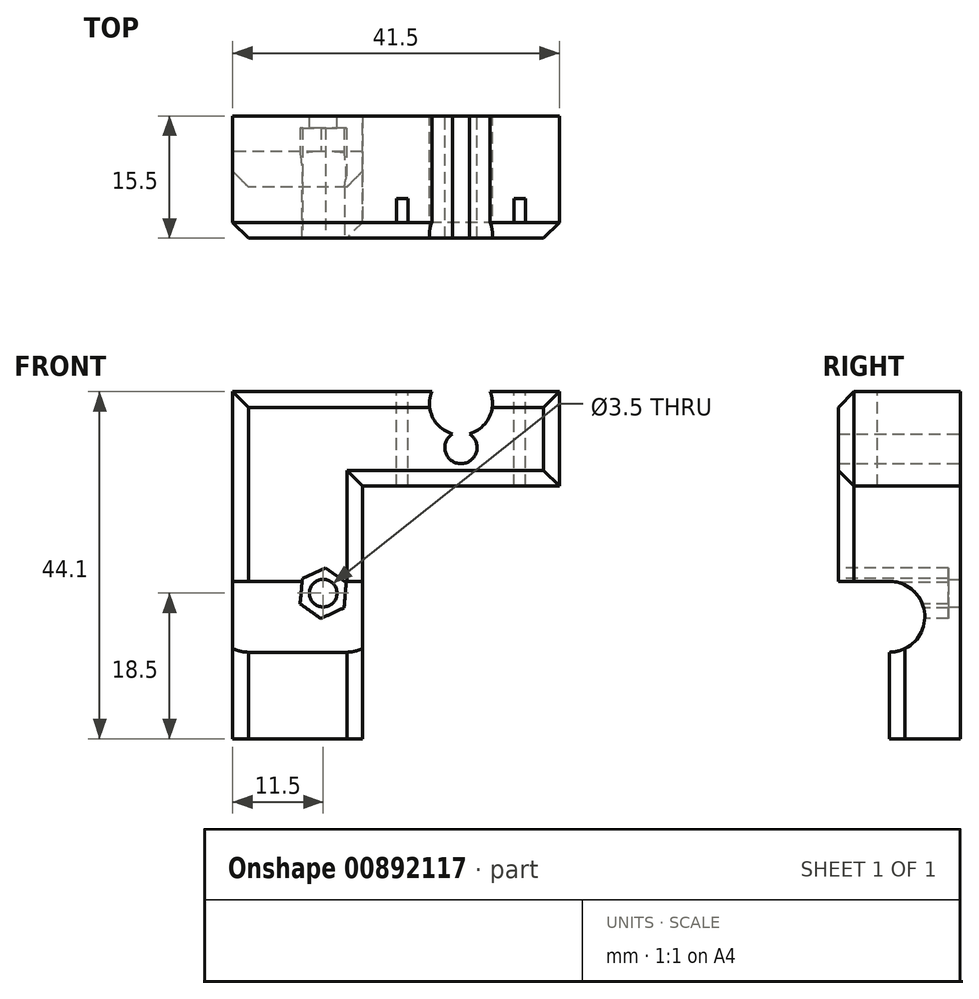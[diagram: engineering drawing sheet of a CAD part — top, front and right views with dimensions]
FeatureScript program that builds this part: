
annotation { "Feature Type Name" : "Feature", "Feature Type Description" : "" }
export const myFeature = defineFeature(function(context is Context, id is Id, definition is map)
    precondition{}
    {
        {
            var Q0;
            Q0=qCreatedBy(makeId("Front.planeOp"),FACE);
            var sketch = newSketch(context, id + "F0", { "sketchPlane" : qUnion([Q0])});
            skLineSegment(sketch, "E0.right", {"start": v(16.5, 21.37) * mm, "end": v(16.5, 38.5) * mm});
            skPoint(sketch, "E1.centerSnap0", {"position": v(8.25, 38.5) * mm});
            skLineSegment(sketch, "E2.trimOffspring", {"start": v(10.09, 38.5) * mm, "end": v(10.09, 38.5) * mm});
            skLineSegment(sketch, "E3", {"start": v(0, 38.5) * mm, "end": v(0, 21.37) * mm});
            skPoint(sketch, "E4.start.orphan", {"position": v(8.25, 33.37) * mm});
            skPoint(sketch, "E5.center.orphan", {"position": v(8.25, 37) * mm});
            skPoint(sketch, "E6.end.orphan", {"position": v(8.25, 21.37) * mm});
            skLineSegment(sketch, "E7", {"start": v(0, 38.5) * mm, "end": v(4.54, 38.5) * mm});
            skArc(sketch, "E8", {"start": v(4.54, 38.5) * mm, "mid": v(4.65, 35.25) * mm, "end": v(7.13, 33.16) * mm});
            skLineSegment(sketch, "E9.trimOffspring", {"start": v(11.96, 38.5) * mm, "end": v(16.5, 38.5) * mm});
            skArc(sketch, "E10", {"start": v(7.13, 33.16) * mm, "mid": v(8.25, 29.4) * mm, "end": v(9.37, 33.16) * mm});
            skArc(sketch, "E11.trimOffspring", {"start": v(9.37, 33.16) * mm, "mid": v(11.85, 35.25) * mm, "end": v(11.96, 38.5) * mm});
            skLineSegment(sketch, "E12", {"start": v(8.25, 21) * mm, "end": v(16.5, 21) * mm});
            skLineSegment(sketch, "E13", {"start": v(16.5, 21) * mm, "end": v(16.5, 21.37) * mm});
            skLineSegment(sketch, "E14", {"start": v(8.25, 21) * mm, "end": v(0, 21) * mm});
            skLineSegment(sketch, "E15", {"start": v(0, 21) * mm, "end": v(0, 21.37) * mm});
            skSolve(sketch);
        }
        {
            var Q0;
            Q0=qSketchRegion(id+"F0",true);
            extrude(context, id + "F1", {"entities" : qUnion([Q0]), "depth" : 17.5 * mm});
        }
        {
            var Q0;
            Q0=makeQuery(id+"F1.opExtrude","CAP_FACE",FACE,{"disambiguationData":[OSD([sQuery(id+"F0.wireOp",EDGE,"E0.right"),sQuery(id+"F0.wireOp",EDGE,"E3"),sQuery(id+"F0.wireOp",EDGE,"E7"),sQuery(id+"F0.wireOp",EDGE,"E8"),sQuery(id+"F0.wireOp",EDGE,"E9.trimOffspring"),sQuery(id+"F0.wireOp",EDGE,"E10"),sQuery(id+"F0.wireOp",EDGE,"E11.trimOffspring"),sQuery(id+"F0.wireOp",EDGE,"E12"),sQuery(id+"F0.wireOp",EDGE,"E13"),sQuery(id+"F0.wireOp",EDGE,"E14"),sQuery(id+"F0.wireOp",EDGE,"E15")])],"isStart":true});
            var sketch = newSketch(context, id + "F2", { "sketchPlane" : qUnion([Q0])});
            skLineSegment(sketch, "E16.bottom", {"start": v(-16.5, 21) * mm, "end": v(0, 21) * mm});
            skLineSegment(sketch, "E16.top", {"start": v(-16.5, 1) * mm, "end": v(0, 1) * mm});
            skLineSegment(sketch, "E16.left", {"start": v(-16.5, 21) * mm, "end": v(-16.5, 1) * mm});
            skLineSegment(sketch, "E16.right", {"start": v(0, 21) * mm, "end": v(0, 1) * mm});
            skSolve(sketch);
        }
        {
            var Q0;
            Q0=makeQuery(id+"F2.imprint","IMPRINT",FACE,{"disambiguationData":[TD([[makeQuery(id+"F2.imprint","IMPRINT",EDGE,{"derivedFrom":sQuery(id+"F2.wireOp",EDGE,"E16.bottom")}),-1.0]])]});
            extrude(context, id + "F3", {"entities" : qUnion([Q0]), "operationType" : NewBodyOperationType.ADD, "oppositeDirection" : true, "depth" : 11 * mm});
        }
        {
            var Q0;
            Q0=makeQuery(id+"F3.boolean.opBoolean","MERGE",FACE,{"derivedFrom":[makeQuery(id+"F1.opExtrude","CAP_FACE",FACE,{"disambiguationData":[OSD([sQuery(id+"F0.wireOp",EDGE,"E0.right"),sQuery(id+"F0.wireOp",EDGE,"E3"),sQuery(id+"F0.wireOp",EDGE,"E7"),sQuery(id+"F0.wireOp",EDGE,"E8"),sQuery(id+"F0.wireOp",EDGE,"E9.trimOffspring"),sQuery(id+"F0.wireOp",EDGE,"E10"),sQuery(id+"F0.wireOp",EDGE,"E11.trimOffspring"),sQuery(id+"F0.wireOp",EDGE,"E12"),sQuery(id+"F0.wireOp",EDGE,"E13"),sQuery(id+"F0.wireOp",EDGE,"E14"),sQuery(id+"F0.wireOp",EDGE,"E15")])],"isStart":true}),makeQuery(id+"F3.opExtrude","CAP_FACE",FACE,{"disambiguationData":[OSD([sQuery(id+"F2.wireOp",EDGE,"E16.bottom"),sQuery(id+"F2.wireOp",EDGE,"E16.top"),sQuery(id+"F2.wireOp",EDGE,"E16.left"),sQuery(id+"F2.wireOp",EDGE,"E16.right")])],"isStart":true})]});
            var sketch = newSketch(context, id + "F4", { "sketchPlane" : qUnion([Q0])});
            skPoint(sketch, "E17.endSnap0", {"position": v(-8.25, 29.4) * mm});
            skCircle(sketch, "E18", {"center": v(-11.5, 19.5) * mm, "radius": 1.75 * mm});
            skPoint(sketch, "E19.orphan", {"position": v(-16.5, 19.5) * mm});
            skPoint(sketch, "E20.end.orphan", {"position": v(-8.25, 19.5) * mm});
            skSolve(sketch);
        }
        {
            var Q0;
            Q0=makeQuery(id+"F3.boolean.opBoolean","MERGE",FACE,{"derivedFrom":[makeQuery(id+"F1.opExtrude","SWEPT_FACE",FACE,{"disambiguationData":[OSD([sQuery(id+"F0.wireOp",EDGE,"E3"),sQuery(id+"F0.wireOp",EDGE,"E15")])]}),makeQuery(id+"F3.opExtrude","SWEPT_FACE",FACE,{"disambiguationData":[OSD([sQuery(id+"F2.wireOp",EDGE,"E16.right")])]})]});
            var sketch = newSketch(context, id + "F5", { "sketchPlane" : qUnion([Q0])});
            skLineSegment(sketch, "E21", {"start": v(11, 21) * mm, "end": v(11, 16.5) * mm});
            skArc(sketch, "E22", {"start": v(11, 21) * mm, "mid": v(6.5, 16.5) * mm, "end": v(11, 12) * mm});
            skLineSegment(sketch, "E23", {"start": v(11, 16.5) * mm, "end": v(11, 12) * mm});
            skPoint(sketch, "E24.orphan", {"position": v(11, 11) * mm});
            skSolve(sketch);
        }
        {
            var Q0;
            Q0=qSketchRegion(id+"F4",true);
            extrude(context, id + "F6", {"entities" : qUnion([Q0]), "operationType" : NewBodyOperationType.REMOVE, "oppositeDirection" : true, "depth" : 22.5 * mm});
        }
        {
            var Q0;
            Q0=makeQuery(id+"F3.opExtrude","CAP_FACE",FACE,{"disambiguationData":[OSD([sQuery(id+"F2.wireOp",EDGE,"E16.bottom"),sQuery(id+"F2.wireOp",EDGE,"E16.top"),sQuery(id+"F2.wireOp",EDGE,"E16.left"),sQuery(id+"F2.wireOp",EDGE,"E16.right")])],"isStart":false});
            var sketch = newSketch(context, id + "F7", { "sketchPlane" : qUnion([Q0])});
            skCircle(sketch, "E25.cCircle", {"center": v(11.5, 19.5) * mm, "radius": 2.8 * mm, "construction": true});
            skLineSegment(sketch, "E25.0", {"start": v(14.43, 20.86) * mm, "end": v(14.14, 17.64) * mm});
            skLineSegment(sketch, "E25.1", {"start": v(14.14, 17.64) * mm, "end": v(11.2, 16.28) * mm});
            skLineSegment(sketch, "E25.2", {"start": v(11.2, 16.28) * mm, "end": v(8.57, 18.14) * mm});
            skLineSegment(sketch, "E25.3", {"start": v(8.57, 18.14) * mm, "end": v(8.86, 21.36) * mm});
            skLineSegment(sketch, "E25.4", {"start": v(8.86, 21.36) * mm, "end": v(11.8, 22.72) * mm});
            skLineSegment(sketch, "E25.5", {"start": v(11.8, 22.72) * mm, "end": v(14.43, 20.86) * mm});
            skPoint(sketch, "E25.0.midPoint", {"position": v(14.29, 19.25) * mm});
            skSolve(sketch);
        }
        {
            var Q0;
            Q0=qSketchRegion(id+"F7",true);
            extrude(context, id + "F8", {"entities" : qUnion([Q0]), "operationType" : NewBodyOperationType.REMOVE, "oppositeDirection" : true, "depth" : 7.5 * mm});
        }
        {
            var Q0;
            Q0=qSketchRegion(id+"F7",true);
            extrude(context, id + "F9", {"entities" : qUnion([Q0]), "operationType" : NewBodyOperationType.REMOVE, "depth" : 13.1 * mm});
        }
        {
            var Q0;
            Q0=qSketchRegion(id+"F5",true);
            extrude(context, id + "F10", {"entities" : qUnion([Q0]), "operationType" : NewBodyOperationType.REMOVE, "oppositeDirection" : true, "depth" : 24.9 * mm});
        }
        {
            var Q0;
            Q0=makeQuery(id+"F3.boolean.opBoolean","MERGE",FACE,{"derivedFrom":[makeQuery(id+"F1.opExtrude","CAP_FACE",FACE,{"disambiguationData":[OSD([sQuery(id+"F0.wireOp",EDGE,"E0.right"),sQuery(id+"F0.wireOp",EDGE,"E3"),sQuery(id+"F0.wireOp",EDGE,"E7"),sQuery(id+"F0.wireOp",EDGE,"E8"),sQuery(id+"F0.wireOp",EDGE,"E9.trimOffspring"),sQuery(id+"F0.wireOp",EDGE,"E10"),sQuery(id+"F0.wireOp",EDGE,"E11.trimOffspring"),sQuery(id+"F0.wireOp",EDGE,"E12"),sQuery(id+"F0.wireOp",EDGE,"E13"),sQuery(id+"F0.wireOp",EDGE,"E14"),sQuery(id+"F0.wireOp",EDGE,"E15")])],"isStart":true}),makeQuery(id+"F3.opExtrude","CAP_FACE",FACE,{"disambiguationData":[OSD([sQuery(id+"F2.wireOp",EDGE,"E16.bottom"),sQuery(id+"F2.wireOp",EDGE,"E16.top"),sQuery(id+"F2.wireOp",EDGE,"E16.left"),sQuery(id+"F2.wireOp",EDGE,"E16.right")])],"isStart":true})]});
            var sketch = newSketch(context, id + "F11", { "sketchPlane" : qUnion([Q0])});
            skLineSegment(sketch, "E26", {"start": v(-16.5, 38.5) * mm, "end": v(-16.5, 1) * mm});
            skLineSegment(sketch, "E27", {"start": v(-16.5, 1) * mm, "end": v(0, 1) * mm});
            skLineSegment(sketch, "E28", {"start": v(0, 1) * mm, "end": v(0, 38.5) * mm});
            skLineSegment(sketch, "E29", {"start": v(0, 38.5) * mm, "end": v(-4.54, 38.5) * mm});
            skLineSegment(sketch, "E30", {"start": v(-11.96, 38.5) * mm, "end": v(-16.5, 38.5) * mm});
            skArc(sketch, "E31", {"start": v(-11.96, 38.5) * mm, "mid": v(-11.85, 35.25) * mm, "end": v(-9.37, 33.16) * mm});
            skArc(sketch, "E32", {"start": v(-9.37, 33.16) * mm, "mid": v(-8.25, 29.4) * mm, "end": v(-7.13, 33.16) * mm});
            skArc(sketch, "E33.trimOffspring", {"start": v(-7.13, 33.16) * mm, "mid": v(-4.65, 35.25) * mm, "end": v(-4.54, 38.5) * mm});
            skSolve(sketch);
        }
        {
            var Q0;
            Q0=makeQuery(id+"F11.imprint","IMPRINT",FACE,{"disambiguationData":[TD([[makeQuery(id+"F11.imprint","IMPRINT",EDGE,{"derivedFrom":sQuery(id+"F11.wireOp",EDGE,"E26")}),-1.0]])]});
            extrude(context, id + "F12", {"entities" : qUnion([Q0]), "operationType" : NewBodyOperationType.REMOVE, "oppositeDirection" : true, "depth" : 2 * mm});
        }
        {
            var Q0;
            Q0=makeQuery(id+"F3.boolean.opBoolean","MERGE",FACE,{"derivedFrom":[makeQuery(id+"F1.opExtrude","SWEPT_FACE",FACE,{"disambiguationData":[OSD([sQuery(id+"F0.wireOp",EDGE,"E0.right"),sQuery(id+"F0.wireOp",EDGE,"E13")])]}),makeQuery(id+"F3.opExtrude","SWEPT_FACE",FACE,{"disambiguationData":[OSD([sQuery(id+"F2.wireOp",EDGE,"E16.left")])]})]});
            var sketch = newSketch(context, id + "F13", { "sketchPlane" : qUnion([Q0])});
            skLineSegment(sketch, "E34.top", {"start": v(-2, 33.1) * mm, "end": v(-17.5, 33.1) * mm});
            skLineSegment(sketch, "E34.left", {"start": v(-2, 38.5) * mm, "end": v(-2, 33.1) * mm});
            skLineSegment(sketch, "E34.right", {"start": v(-17.5, 38.5) * mm, "end": v(-17.5, 33.1) * mm});
            skLineSegment(sketch, "E35.top", {"start": v(-2, 45.1) * mm, "end": v(-17.5, 45.1) * mm});
            skLineSegment(sketch, "E35.left", {"start": v(-2, 38.5) * mm, "end": v(-2, 45.1) * mm});
            skLineSegment(sketch, "E35.right", {"start": v(-17.5, 38.5) * mm, "end": v(-17.5, 45.1) * mm});
            skSolve(sketch);
        }
        {
            var Q0;
            Q0=makeQuery(id+"F13.imprint","IMPRINT",FACE,{"disambiguationData":[TD([[makeQuery(id+"F13.imprint","IMPRINT",EDGE,{"derivedFrom":sQuery(id+"F13.wireOp",EDGE,"E35.top")}),1.0]])]});
            var Q1;
            Q1=makeQuery(id+"F13.imprint","IMPRINT",FACE,{"disambiguationData":[TD([[makeQuery(id+"F13.imprint","IMPRINT",EDGE,{"derivedFrom":sQuery(id+"F13.wireOp",EDGE,"E34.top")}),-1.0]])]});
            extrude(context, id + "F14", {"entities" : qUnion([Q0, Q1]), "operationType" : NewBodyOperationType.ADD, "depth" : 25 * mm});
        }
        {
            var Q0;
            Q0=makeQuery(id+"F14.opExtrude","CAP_FACE",FACE,{"disambiguationData":[OSD([sQuery(id+"F13.wireOp",EDGE,"E34.top"),sQuery(id+"F13.wireOp",EDGE,"E34.left"),sQuery(id+"F13.wireOp",EDGE,"E34.right"),sQuery(id+"F13.wireOp",EDGE,"E35.top"),sQuery(id+"F13.wireOp",EDGE,"E35.left"),sQuery(id+"F13.wireOp",EDGE,"E35.right")])],"isStart":true});
            extrude(context, id + "F15", {"entities" : qUnion([Q0]), "operationType" : NewBodyOperationType.ADD, "depth" : 16.5 * mm});
        }
        {
            var Q0;
            {var subQ0=sQuery(id+"F13.wireOp",EDGE,"E35.left");var subQ1=sQuery(id+"F13.wireOp",EDGE,"E34.left");Q0=makeQuery(id+"F15.boolean.opBoolean","MERGE",FACE,{"derivedFrom":[makeQuery(id+"F14.boolean.opBoolean","MERGE",FACE,{"derivedFrom":[makeQuery(id+"F12.boolean.opBoolean","COPY",FACE,{"derivedFrom":makeQuery(id+"F12.opExtrude","CAP_FACE",FACE,{"disambiguationData":[OSD([sQuery(id+"F4.wireOp",EDGE,"E18"),sQuery(id+"F11.wireOp",EDGE,"E26"),sQuery(id+"F11.wireOp",EDGE,"E27"),sQuery(id+"F11.wireOp",EDGE,"E28"),sQuery(id+"F11.wireOp",EDGE,"E29"),sQuery(id+"F11.wireOp",EDGE,"E30"),sQuery(id+"F11.wireOp",EDGE,"E31"),sQuery(id+"F11.wireOp",EDGE,"E32"),sQuery(id+"F11.wireOp",EDGE,"E33.trimOffspring")])],"isStart":false})}),makeQuery(id+"F14.opExtrude","SWEPT_FACE",FACE,{"disambiguationData":[OSD([subQ1,subQ0])]})]}),makeQuery(id+"F15.opExtrude","SWEPT_FACE",FACE,{"disambiguationData":[OSD([subQ1,subQ0])]})]});}
            var sketch = newSketch(context, id + "F16", { "sketchPlane" : qUnion([Q0])});
            skPoint(sketch, "E36.endSnap0", {"position": v(-29, 45.1) * mm});
            skArc(sketch, "E37", {"start": v(-27.93, 39.74) * mm, "mid": v(-25.4, 41.83) * mm, "end": v(-25.3, 45.1) * mm});
            skPoint(sketch, "E36.start.orphan", {"position": v(-29, 45.1) * mm});
            skArc(sketch, "E38", {"start": v(-30.07, 39.74) * mm, "mid": v(-29, 35.94) * mm, "end": v(-27.93, 39.74) * mm});
            skArc(sketch, "E39.trimOffspring", {"start": v(-32.7, 45.1) * mm, "mid": v(-32.6, 41.83) * mm, "end": v(-30.07, 39.74) * mm});
            skPoint(sketch, "E40.trimOffspring.end.orphan", {"position": v(-41.5, 45.1) * mm});
            skPoint(sketch, "E41.start.orphan", {"position": v(-16.5, 45.1) * mm});
            skLineSegment(sketch, "E42", {"start": v(-32.7, 45.1) * mm, "end": v(-25.3, 45.1) * mm});
            skSolve(sketch);
        }
        {
            var Q0;
            Q0=qSketchRegion(id+"F16",true);
            extrude(context, id + "F17", {"entities" : qUnion([Q0]), "operationType" : NewBodyOperationType.REMOVE, "oppositeDirection" : true, "depth" : 25 * mm});
        }
        {
            var Q0;
            {var subQ6=sQuery(id+"F13.wireOp",EDGE,"E35.top");Q0=makeQuery(id+"F17.boolean.opBoolean","SPLIT",FACE,{"disambiguationData":[TD([makeQuery(id+"F3.opExtrude","SWEPT_FACE",FACE,{"disambiguationData":[OSD([sQuery(id+"F2.wireOp",EDGE,"E16.right")])]})])],"derivedFrom":makeQuery(id+"F15.boolean.opBoolean","MERGE",FACE,{"derivedFrom":[makeQuery(id+"F14.opExtrude","SWEPT_FACE",FACE,{"disambiguationData":[OSD([subQ6])]}),makeQuery(id+"F15.opExtrude","SWEPT_FACE",FACE,{"disambiguationData":[OSD([subQ6])]})]})});}
            var sketch = newSketch(context, id + "F18", { "sketchPlane" : qUnion([Q0])});
            skLineSegment(sketch, "E43.bottom", {"start": v(20.8, -12.5) * mm, "end": v(22.3, -12.5) * mm});
            skLineSegment(sketch, "E43.top", {"start": v(20.8, -15.5) * mm, "end": v(22.3, -15.5) * mm});
            skLineSegment(sketch, "E43.left", {"start": v(20.8, -12.5) * mm, "end": v(20.8, -15.5) * mm});
            skLineSegment(sketch, "E43.right", {"start": v(22.3, -12.5) * mm, "end": v(22.3, -15.5) * mm});
            skLineSegment(sketch, "E44.bottom", {"start": v(35.7, -12.5) * mm, "end": v(37.2, -12.5) * mm});
            skLineSegment(sketch, "E44.top", {"start": v(35.7, -15.5) * mm, "end": v(37.2, -15.5) * mm});
            skLineSegment(sketch, "E44.left", {"start": v(35.7, -12.5) * mm, "end": v(35.7, -15.5) * mm});
            skLineSegment(sketch, "E44.right", {"start": v(37.2, -12.5) * mm, "end": v(37.2, -15.5) * mm});
            skSolve(sketch);
        }
        {
            var Q0;
            Q0=qSketchRegion(id+"F18",true);
            extrude(context, id + "F19", {"entities" : qUnion([Q0]), "operationType" : NewBodyOperationType.REMOVE, "oppositeDirection" : true, "depth" : 25 * mm});
        }
        {
            var Q0;
            {var subQ0=sQuery(id+"F13.wireOp",EDGE,"E35.right");var subQ1=sQuery(id+"F13.wireOp",EDGE,"E34.right");Q0=makeQuery(id+"F15.boolean.opBoolean","MERGE",FACE,{"derivedFrom":[makeQuery(id+"F14.boolean.opBoolean","MERGE",FACE,{"derivedFrom":[makeQuery(id+"F1.opExtrude","CAP_FACE",FACE,{"disambiguationData":[OSD([sQuery(id+"F0.wireOp",EDGE,"E0.right"),sQuery(id+"F0.wireOp",EDGE,"E3"),sQuery(id+"F0.wireOp",EDGE,"E7"),sQuery(id+"F0.wireOp",EDGE,"E8"),sQuery(id+"F0.wireOp",EDGE,"E9.trimOffspring"),sQuery(id+"F0.wireOp",EDGE,"E10"),sQuery(id+"F0.wireOp",EDGE,"E11.trimOffspring"),sQuery(id+"F0.wireOp",EDGE,"E12"),sQuery(id+"F0.wireOp",EDGE,"E13"),sQuery(id+"F0.wireOp",EDGE,"E14"),sQuery(id+"F0.wireOp",EDGE,"E15")])],"isStart":false}),makeQuery(id+"F14.opExtrude","SWEPT_FACE",FACE,{"disambiguationData":[OSD([subQ1,subQ0])]})]}),makeQuery(id+"F15.opExtrude","SWEPT_FACE",FACE,{"disambiguationData":[OSD([subQ1,subQ0])]})]});}
            var sketch = newSketch(context, id + "F20", { "sketchPlane" : qUnion([Q0])});
            skPoint(sketch, "E45.1", {"position": v(8.25, 38.5) * mm});
            skLineSegment(sketch, "E45.2", {"start": v(10.09, 38.5) * mm, "end": v(10.09, 38.5) * mm});
            skLineSegment(sketch, "E45.3", {"start": v(10.09, 38.5) * mm, "end": v(10.09, 38.5) * mm});
            skLineSegment(sketch, "E45.4", {"start": v(10.09, 38.5) * mm, "end": v(10.09, 38.5) * mm});
            skPoint(sketch, "E45.6", {"position": v(8.25, 33.37) * mm});
            skPoint(sketch, "E45.7", {"position": v(8.25, 37) * mm});
            skPoint(sketch, "E45.8", {"position": v(8.25, 21.37) * mm});
            skArc(sketch, "E45.10", {"start": v(4.54, 38.5) * mm, "mid": v(4.65, 35.25) * mm, "end": v(7.13, 33.16) * mm});
            skLineSegment(sketch, "E45.11", {"start": v(10.09, 38.5) * mm, "end": v(10.09, 38.5) * mm});
            skArc(sketch, "E45.13", {"start": v(7.13, 33.16) * mm, "mid": v(8.25, 29.4) * mm, "end": v(9.37, 33.16) * mm});
            skArc(sketch, "E45.14", {"start": v(9.37, 33.16) * mm, "mid": v(11.85, 35.25) * mm, "end": v(11.96, 38.5) * mm});
            skPoint(sketch, "E45.5.end.orphan", {"position": v(0, 21.37) * mm});
            skPoint(sketch, "E45.5.start.orphan", {"position": v(0, 38.5) * mm});
            skPoint(sketch, "E45.9.end.orphan", {"position": v(4.54, 38.5) * mm});
            skPoint(sketch, "E45.9.start.orphan", {"position": v(0, 38.5) * mm});
            skPoint(sketch, "E45.12.end.orphan", {"position": v(16.5, 38.5) * mm});
            skPoint(sketch, "E45.12.start.orphan", {"position": v(11.96, 38.5) * mm});
            skPoint(sketch, "E45.0.end.orphan", {"position": v(16.5, 38.5) * mm});
            skPoint(sketch, "E45.0.start.orphan", {"position": v(16.5, 21.37) * mm});
            skPoint(sketch, "E45.17.end.orphan", {"position": v(0, 21) * mm});
            skPoint(sketch, "E45.17.start.orphan", {"position": v(8.25, 21) * mm});
            skPoint(sketch, "E45.15.end.orphan", {"position": v(16.5, 21) * mm});
            skPoint(sketch, "E45.15.start.orphan", {"position": v(8.25, 21) * mm});
            skPoint(sketch, "E45.16.end.orphan", {"position": v(16.5, 21.37) * mm});
            skPoint(sketch, "E45.16.start.orphan", {"position": v(16.5, 21) * mm});
            skPoint(sketch, "E45.18.end.orphan", {"position": v(0, 21.37) * mm});
            skPoint(sketch, "E45.18.start.orphan", {"position": v(0, 21) * mm});
            skLineSegment(sketch, "E46", {"start": v(4.54, 38.5) * mm, "end": v(11.96, 38.5) * mm});
            skSolve(sketch);
        }
        {
            var Q0;
            {var subQ1=sQuery(id+"F20.wireOp",EDGE,"E45.10");Q0=makeQuery(id+"F20.imprint","IMPRINT",FACE,{"disambiguationData":[TD([[makeQuery(id+"F20.imprint","IMPRINT",EDGE,{"derivedFrom":subQ1}),1.0]])]});}
            extrude(context, id + "F21", {"entities" : qUnion([Q0]), "operationType" : NewBodyOperationType.ADD, "oppositeDirection" : true, "depth" : 15.5 * mm});
        }
        {
            var Q0;
            Q0=makeQuery(id+"F14.opExtrude","CAP_EDGE",EDGE,{"disambiguationData":[OSD([sQuery(id+"F13.wireOp",EDGE,"E34.right"),sQuery(id+"F13.wireOp",EDGE,"E35.right")])],"isStart":false});
            var Q1;
            Q1=makeQuery(id+"F15.boolean.opBoolean","MERGE",EDGE,{"derivedFrom":[makeQuery(id+"F1.opExtrude","CAP_EDGE",EDGE,{"disambiguationData":[OSD([sQuery(id+"F0.wireOp",EDGE,"E3"),sQuery(id+"F0.wireOp",EDGE,"E15")])],"isStart":false}),makeQuery(id+"F15.opExtrude","CAP_EDGE",EDGE,{"disambiguationData":[OSD([sQuery(id+"F13.wireOp",EDGE,"E34.right"),sQuery(id+"F13.wireOp",EDGE,"E35.right")])],"isStart":false})]});
            var Q2;
            Q2=makeQuery(id+"F1.opExtrude","CAP_EDGE",EDGE,{"disambiguationData":[OSD([sQuery(id+"F0.wireOp",EDGE,"E0.right"),sQuery(id+"F0.wireOp",EDGE,"E13")])],"isStart":false});
            var Q3;
            Q3=makeQuery(id+"F14.opExtrude","SWEPT_EDGE",EDGE,{"disambiguationData":[OSD([sQuery(id+"F0.wireOp",EDGE,"E0.right"),sQuery(id+"F0.wireOp",EDGE,"E13"),sQuery(id+"F13.wireOp",EDGE,"E34.top"),sQuery(id+"F13.wireOp",EDGE,"E34.right")])]});
            var Q4;
            {var subQ0=sQuery(id+"F13.wireOp",EDGE,"E35.right");var subQ2=sQuery(id+"F13.wireOp",EDGE,"E35.top");Q4=makeQuery(id+"F17.boolean.opBoolean","SPLIT",EDGE,{"disambiguationData":[TD([makeQuery(id+"F3.opExtrude","SWEPT_FACE",FACE,{"disambiguationData":[OSD([sQuery(id+"F2.wireOp",EDGE,"E16.right")])]})])],"derivedFrom":makeQuery(id+"F15.boolean.opBoolean","MERGE",EDGE,{"derivedFrom":[makeQuery(id+"F14.opExtrude","SWEPT_EDGE",EDGE,{"disambiguationData":[OSD([subQ2,subQ0])]}),makeQuery(id+"F15.opExtrude","SWEPT_EDGE",EDGE,{"disambiguationData":[OSD([subQ2,subQ0])]})]})});}
            var Q5;
            {var subQ0=sQuery(id+"F13.wireOp",EDGE,"E35.top");var subQ1=sQuery(id+"F13.wireOp",EDGE,"E35.right");Q5=makeQuery(id+"F17.boolean.opBoolean","SPLIT",EDGE,{"disambiguationData":[TD([makeQuery(id+"F17.opExtrude","SWEPT_FACE",FACE,{"disambiguationData":[OSD([sQuery(id+"F16.wireOp",EDGE,"E39.trimOffspring")])]})])],"derivedFrom":makeQuery(id+"F15.boolean.opBoolean","MERGE",EDGE,{"derivedFrom":[makeQuery(id+"F14.opExtrude","SWEPT_EDGE",EDGE,{"disambiguationData":[OSD([subQ0,subQ1])]}),makeQuery(id+"F15.opExtrude","SWEPT_EDGE",EDGE,{"disambiguationData":[OSD([subQ0,subQ1])]})]})});}
            chamfer(context, id + "F22", {"entities" : qUnion([Q0, Q1, Q2, Q3, Q4, Q5]), "width" : 2 * mm, "tangentPropagation" : true});
        }
        {
            var Q0;
            Q0=makeQuery(id+"F3.opExtrude","CAP_EDGE",EDGE,{"disambiguationData":[OSD([sQuery(id+"F2.wireOp",EDGE,"E16.right")])],"isStart":false});
            var Q1;
            Q1=makeQuery(id+"F3.opExtrude","CAP_EDGE",EDGE,{"disambiguationData":[OSD([sQuery(id+"F2.wireOp",EDGE,"E16.left")])],"isStart":false});
            chamfer(context, id + "F23", {"entities" : qUnion([Q0, Q1]), "width" : 2 * mm, "tangentPropagation" : true});
        }
    });
